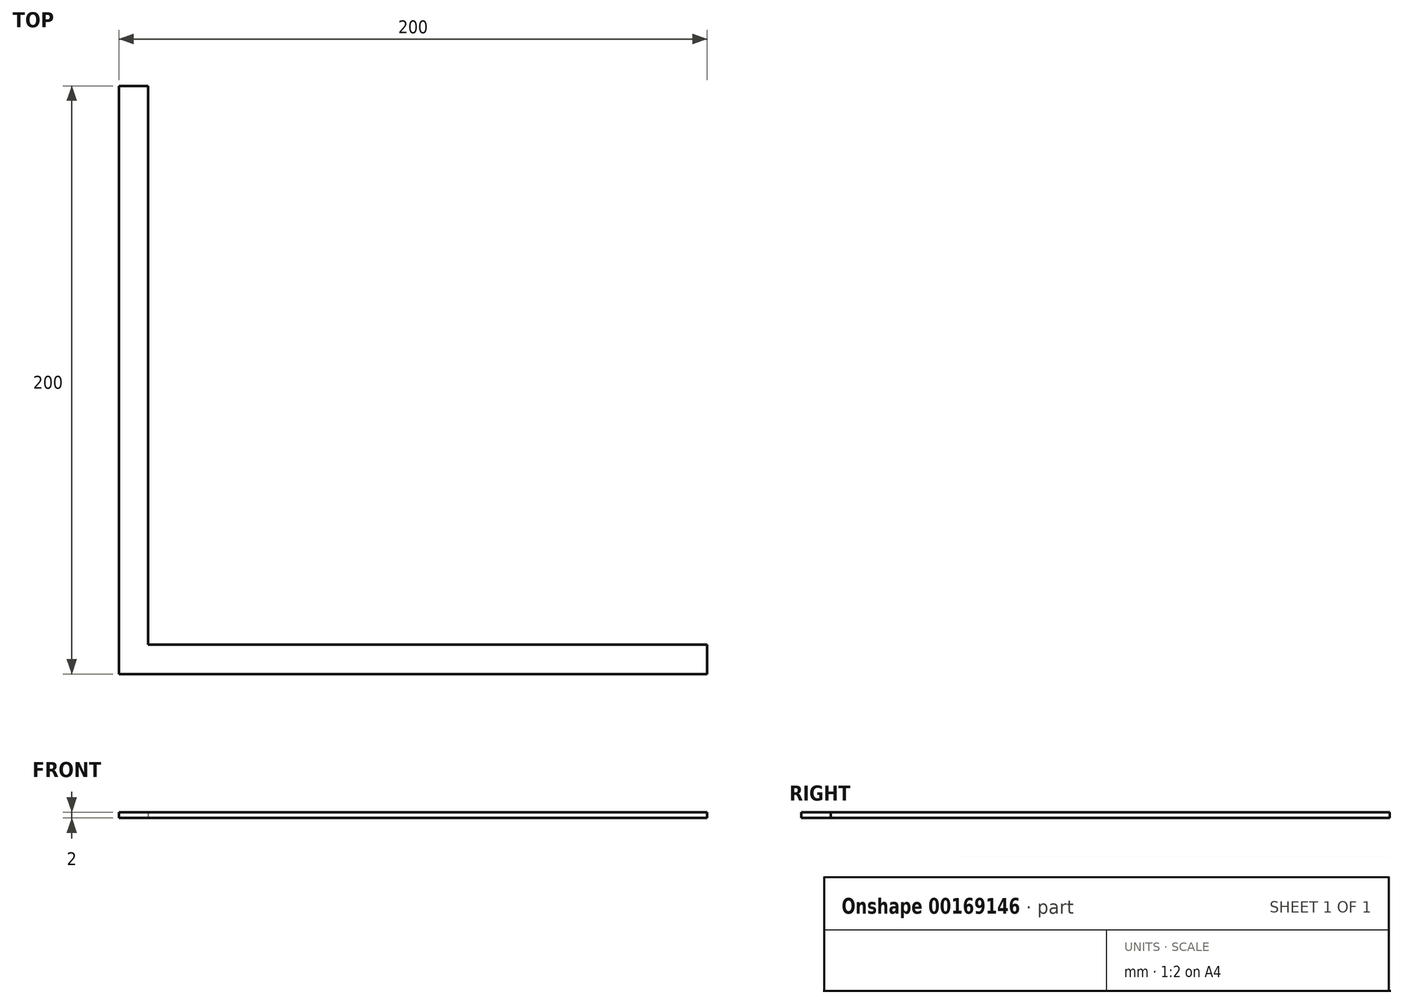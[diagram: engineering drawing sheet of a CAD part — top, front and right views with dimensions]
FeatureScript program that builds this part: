
annotation { "Feature Type Name" : "Feature", "Feature Type Description" : "" }
export const myFeature = defineFeature(function(context is Context, id is Id, definition is map)
    precondition{}
    {
        {
            var Q0;
            Q0=qCreatedBy(makeId("Top.planeOp"),FACE);
            var sketch = newSketch(context, id + "F0", { "sketchPlane" : qUnion([Q0])});
            skLineSegment(sketch, "E0.bottom", {"start": v(0, 0) * mm, "end": v(10, 0) * mm});
            skLineSegment(sketch, "E0.top", {"start": v(0, 200) * mm, "end": v(10, 200) * mm});
            skLineSegment(sketch, "E0.left", {"start": v(0, 0) * mm, "end": v(0, 200) * mm});
            skLineSegment(sketch, "E0.right", {"start": v(10, 0) * mm, "end": v(10, 200) * mm});
            skLineSegment(sketch, "E1.bottom", {"start": v(0, 0) * mm, "end": v(200, 0) * mm});
            skLineSegment(sketch, "E1.top", {"start": v(0, 10) * mm, "end": v(200, 10) * mm});
            skLineSegment(sketch, "E1.left", {"start": v(0, 0) * mm, "end": v(0, 10) * mm});
            skLineSegment(sketch, "E1.right", {"start": v(200, 0) * mm, "end": v(200, 10) * mm});
            skSolve(sketch);
        }
        {
            var Q0;
            Q0=qSketchRegion(id+"F0",true);
            extrude(context, id + "F1", {"entities" : qUnion([Q0]), "depth" : 2 * mm});
        }
    });
